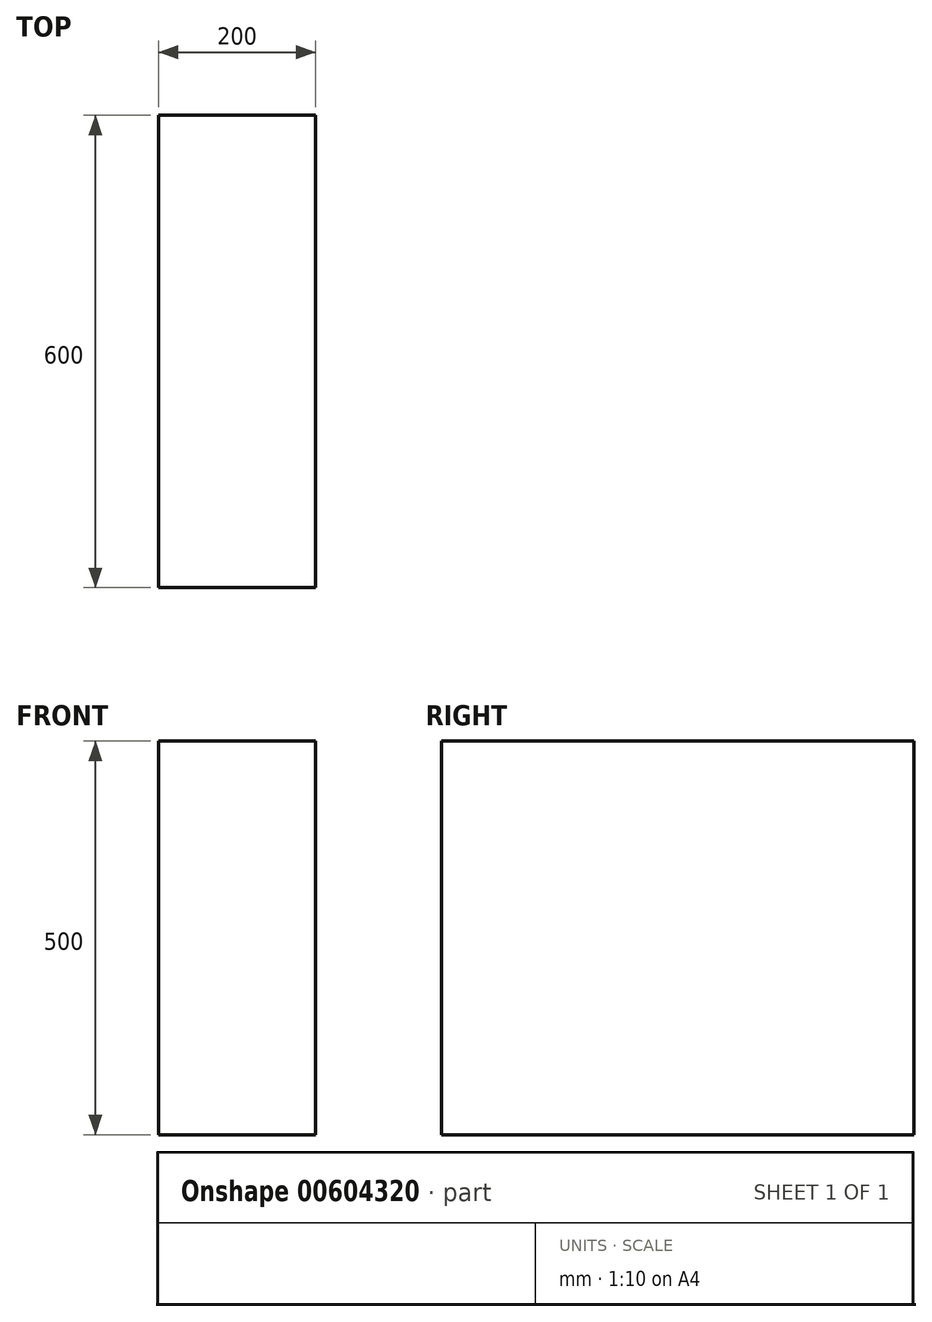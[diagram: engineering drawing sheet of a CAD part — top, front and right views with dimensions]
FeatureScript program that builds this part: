
annotation { "Feature Type Name" : "Feature", "Feature Type Description" : "" }
export const myFeature = defineFeature(function(context is Context, id is Id, definition is map)
    precondition{}
    {
        {
            var Q0;
            Q0=qCreatedBy(makeId("Front.planeOp"),FACE);
            var sketch = newSketch(context, id + "F0", { "sketchPlane" : qUnion([Q0])});
            skLineSegment(sketch, "E0.bottom", {"start": v(100, -250) * mm, "end": v(-100, -250) * mm});
            skLineSegment(sketch, "E0.top", {"start": v(100, 250) * mm, "end": v(-100, 250) * mm});
            skLineSegment(sketch, "E0.left", {"start": v(100, -250) * mm, "end": v(100, 250) * mm});
            skLineSegment(sketch, "E0.right", {"start": v(-100, -250) * mm, "end": v(-100, 250) * mm});
            skPoint(sketch, "E0.middle", {"position": v(0, 0) * mm});
            skSolve(sketch);
        }
        {
            var Q0;
            Q0 = qSketchRegion(id + "F0", true);
            extrude(context, id + "F1", {"entities" : qUnion([Q0]), "endBound" : BoundingType.SYMMETRIC, "depth" : 600 * mm, "offsetDistance" : 25 * mm});
        }
    });
